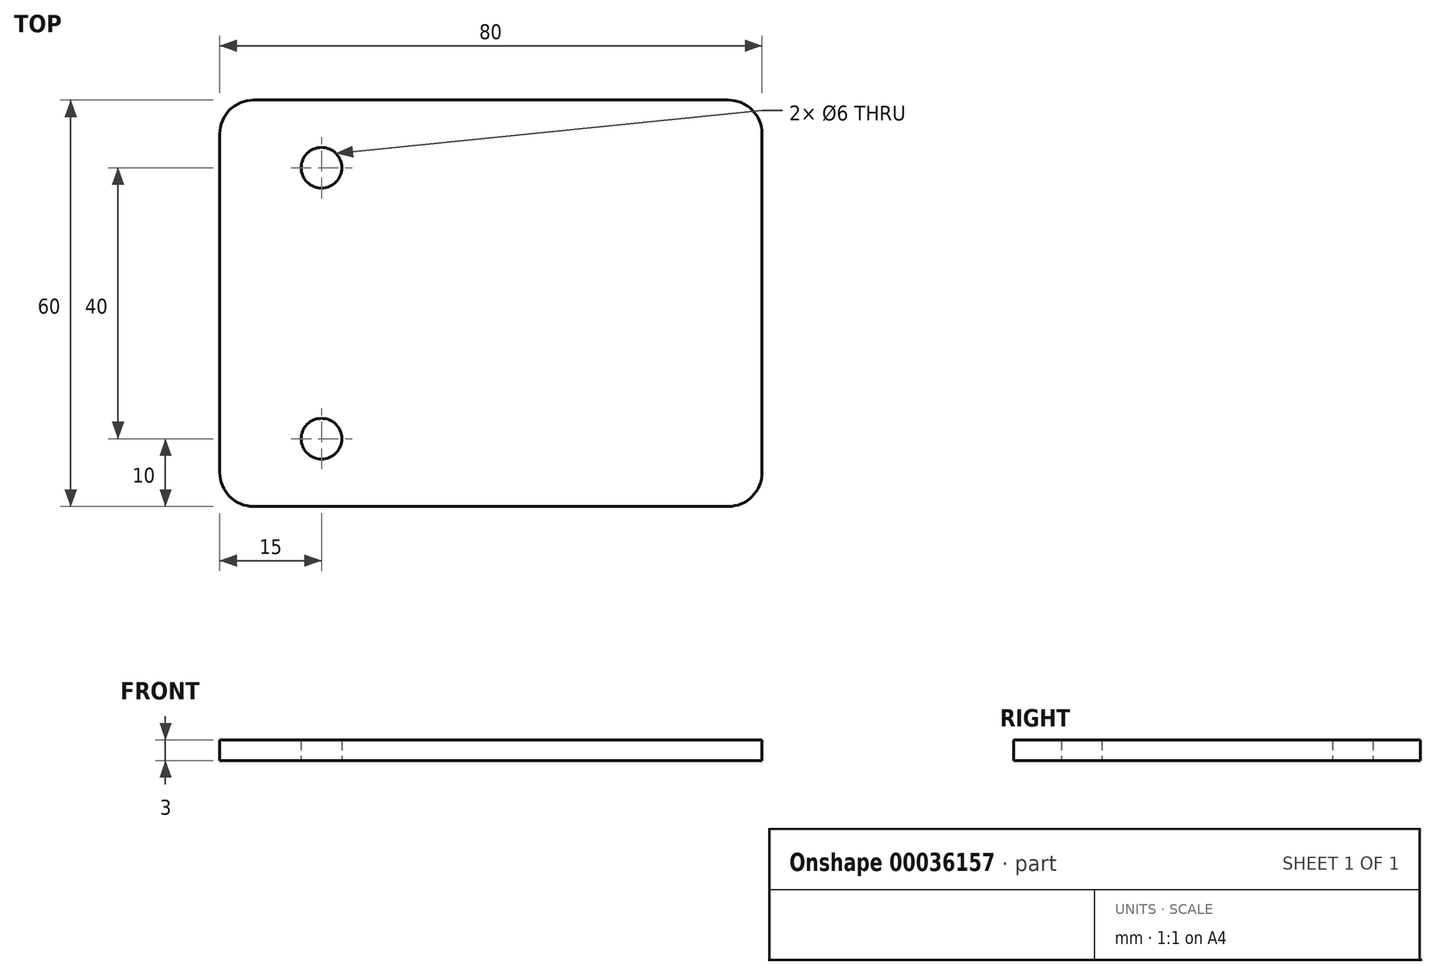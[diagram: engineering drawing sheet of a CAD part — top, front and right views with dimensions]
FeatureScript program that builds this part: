
annotation { "Feature Type Name" : "Feature", "Feature Type Description" : "" }
export const myFeature = defineFeature(function(context is Context, id is Id, definition is map)
    precondition{}
    {
        {
            var Q0;
            Q0=qCreatedBy(makeId("Top.planeOp"),FACE);
            var sketch = newSketch(context, id + "F0", { "sketchPlane" : qUnion([Q0])});
            skLineSegment(sketch, "E0.rect.bottom", {"start": v(35, -30) * mm, "end": v(-35, -30) * mm});
            skLineSegment(sketch, "E0.rect.top", {"start": v(35, 30) * mm, "end": v(-35, 30) * mm});
            skLineSegment(sketch, "E0.rect.left", {"start": v(40, -25) * mm, "end": v(40, 25) * mm});
            skLineSegment(sketch, "E0.rect.right", {"start": v(-40, -25) * mm, "end": v(-40, 25) * mm});
            skPoint(sketch, "E0.rect.middle", {"position": v(0, 0) * mm});
            skPoint(sketch, "E1.visualSharp", {"position": v(-40, 30) * mm});
            skArc(sketch, "E1.filletArc", {"start": v(-35, 30) * mm, "mid": v(-38.54, 28.54) * mm, "end": v(-40, 25) * mm});
            skPoint(sketch, "E2.visualSharp", {"position": v(40, -30) * mm});
            skArc(sketch, "E2.filletArc", {"start": v(35, -30) * mm, "mid": v(38.54, -28.54) * mm, "end": v(40, -25) * mm});
            skPoint(sketch, "E3.visualSharp", {"position": v(40, 30) * mm});
            skArc(sketch, "E3.filletArc", {"start": v(40, 25) * mm, "mid": v(38.54, 28.54) * mm, "end": v(35, 30) * mm});
            skPoint(sketch, "E4.visualSharp", {"position": v(-40, -30) * mm});
            skArc(sketch, "E4.filletArc", {"start": v(-40, -25) * mm, "mid": v(-38.54, -28.54) * mm, "end": v(-35, -30) * mm});
            skCircle(sketch, "E5", {"center": v(-25, 20) * mm, "radius": 3 * mm});
            skLineSegment(sketch, "E6", {"start": v(-25, 20) * mm, "end": v(-25, -20) * mm, "construction": true});
            skCircle(sketch, "E7", {"center": v(-25, -20) * mm, "radius": 3 * mm});
            skSolve(sketch);
        }
        {
            var Q0;
            Q0 = qSketchRegion(id + "F0", true);
            extrude(context, id + "F1", {"entities" : qUnion([Q0]), "depth" : 3 * mm});
        }
    });
